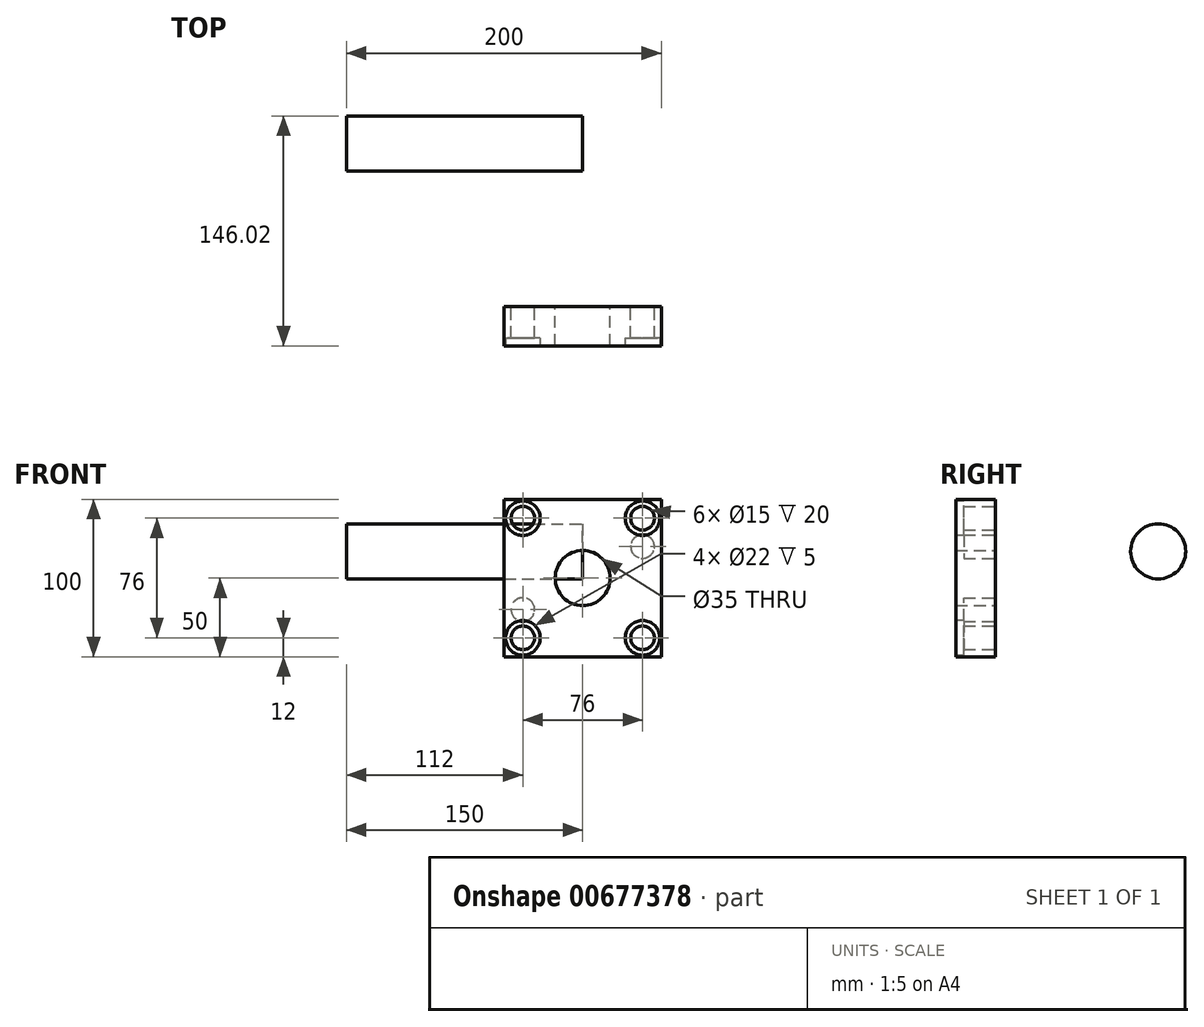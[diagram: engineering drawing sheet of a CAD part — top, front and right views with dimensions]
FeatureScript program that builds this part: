
annotation { "Feature Type Name" : "Feature", "Feature Type Description" : "" }
export const myFeature = defineFeature(function(context is Context, id is Id, definition is map)
    precondition{}
    {
        {
            var Q0;
            Q0=qCreatedBy(makeId("Front.planeOp"),FACE);
            var sketch = newSketch(context, id + "F0", { "sketchPlane" : qUnion([Q0])});
            skLineSegment(sketch, "E0.bottom", {"start": v(50, 50) * mm, "end": v(-50, 50) * mm});
            skLineSegment(sketch, "E0.top", {"start": v(50, -50) * mm, "end": v(-50, -50) * mm});
            skLineSegment(sketch, "E0.left", {"start": v(50, 50) * mm, "end": v(50, -50) * mm});
            skLineSegment(sketch, "E0.right", {"start": v(-50, 50) * mm, "end": v(-50, -50) * mm});
            skPoint(sketch, "E0.middle", {"position": v(0, 0) * mm});
            skCircle(sketch, "E1", {"center": v(0, 0) * mm, "radius": 17.5 * mm});
            skCircle(sketch, "E2", {"center": v(38, 38) * mm, "radius": 7.5 * mm});
            skCircle(sketch, "E3.1.0", {"center": v(-38, 38) * mm, "radius": 7.5 * mm});
            skCircle(sketch, "E3.2.0", {"center": v(-38, -38) * mm, "radius": 7.5 * mm});
            skCircle(sketch, "E3.3.0", {"center": v(38, -38) * mm, "radius": 7.5 * mm});
            skSolve(sketch);
        }
        {
            var Q0;
            Q0=qSketchRegion(id+"F0",true);
            extrude(context, id + "F1", {"entities" : qUnion([Q0]), "depth" : 25 * mm, "offsetDistance" : 25 * mm});
        }
        {
            var Q0;
            Q0=qCreatedBy(makeId("Right.planeOp"),FACE);
            var sketch = newSketch(context, id + "F2", { "sketchPlane" : qUnion([Q0])});
            skCircle(sketch, "E4", {"center": v(103.52, 16.97) * mm, "radius": 17.5 * mm});
            skSolve(sketch);
        }
        {
            var Q0;
            Q0=qSketchRegion(id+"F2",true);
            extrude(context, id + "F3", {"entities" : qUnion([Q0]), "oppositeDirection" : true, "depth" : 150 * mm, "offsetDistance" : 25 * mm});
        }
        {
            var Q0;
            Q0=makeQuery(id+"F1.opExtrude","CAP_FACE",FACE,{"disambiguationData":[OSD([sQuery(id+"F0.wireOp",EDGE,"E0.bottom"),sQuery(id+"F0.wireOp",EDGE,"E0.top"),sQuery(id+"F0.wireOp",EDGE,"E0.left"),sQuery(id+"F0.wireOp",EDGE,"E0.right"),sQuery(id+"F0.wireOp",EDGE,"E1"),sQuery(id+"F0.wireOp",EDGE,"E2"),sQuery(id+"F0.wireOp",EDGE,"E3.1.0"),sQuery(id+"F0.wireOp",EDGE,"E3.2.0"),sQuery(id+"F0.wireOp",EDGE,"E3.3.0")])],"isStart":false});
            var sketch = newSketch(context, id + "F4", { "sketchPlane" : qUnion([Q0])});
            skCircle(sketch, "E5.0", {"center": v(38, 38) * mm, "radius": 7.5 * mm});
            skCircle(sketch, "E6.0", {"center": v(-38, 38) * mm, "radius": 7.5 * mm});
            skCircle(sketch, "E7.0", {"center": v(-38, -38) * mm, "radius": 7.5 * mm});
            skCircle(sketch, "E8.0", {"center": v(38, -38) * mm, "radius": 7.5 * mm});
            skCircle(sketch, "E9", {"center": v(38, 38) * mm, "radius": 11 * mm});
            skCircle(sketch, "E10.1.0", {"center": v(-38, 38) * mm, "radius": 11 * mm});
            skCircle(sketch, "E10.2.0", {"center": v(-38, -38) * mm, "radius": 11 * mm});
            skCircle(sketch, "E10.3.0", {"center": v(38, -38) * mm, "radius": 11 * mm});
            skPoint(sketch, "E10.center", {"position": v(0, 0) * mm});
            skSolve(sketch);
        }
        {
            var Q0;
            Q0 = qSketchRegion(id + "F4", true);
            extrude(context, id + "F5", {"entities" : qUnion([Q0]), "operationType" : NewBodyOperationType.REMOVE, "oppositeDirection" : true, "depth" : 5 * mm, "offsetDistance" : 25 * mm});
        }
        {
            var Q0;
            Q0=makeQuery(id+"F1.opExtrude","CAP_FACE",FACE,{"disambiguationData":[OSD([sQuery(id+"F0.wireOp",EDGE,"E0.bottom"),sQuery(id+"F0.wireOp",EDGE,"E0.top"),sQuery(id+"F0.wireOp",EDGE,"E0.left"),sQuery(id+"F0.wireOp",EDGE,"E0.right"),sQuery(id+"F0.wireOp",EDGE,"E1"),sQuery(id+"F0.wireOp",EDGE,"E2"),sQuery(id+"F0.wireOp",EDGE,"E3.1.0"),sQuery(id+"F0.wireOp",EDGE,"E3.2.0"),sQuery(id+"F0.wireOp",EDGE,"E3.3.0")])],"isStart":true});
            var sketch = newSketch(context, id + "F6", { "sketchPlane" : qUnion([Q0])});
            skCircle(sketch, "E11", {"center": v(-38, 20) * mm, "radius": 7.5 * mm});
            skCircle(sketch, "E12", {"center": v(38, -20) * mm, "radius": 7.5 * mm});
            skSolve(sketch);
        }
        {
            var Q0;
            Q0 = qSketchRegion(id + "F6", true);
            extrude(context, id + "F7", {"entities" : qUnion([Q0]), "operationType" : NewBodyOperationType.REMOVE, "oppositeDirection" : true, "depth" : 20 * mm, "offsetDistance" : 25 * mm});
        }
    });
